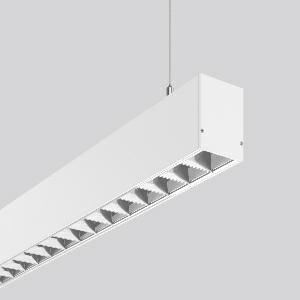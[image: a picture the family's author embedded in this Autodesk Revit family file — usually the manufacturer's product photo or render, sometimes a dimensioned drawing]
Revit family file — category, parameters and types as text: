
# Revit family: less_is_more_50_312342_002_1_76_e1d1
name_source: partatom
category: Lighting Fixtures
units: mm (PartAtom-declared; Revit-internal decimal feet)

## family parameters
Cut with Voids When Loaded = No
Host = Face
Light Source = No
Part Type = Normal
Room Calculation Point = No
Round Connector Dimension = Use Diameter
Shared = No

## types (1)
- LESS IS MORE 50 (1 x LED Modul 840, 5050 lm, 4000)
    Apparent Load = 46 VA
    CIE Flux Codes = 95 100 100 63 100
    Color Rendering = 80
    Color Temperature = 4000
    Default Elevation = 1800 mm
    Description = Series: LESS IS MORE 50
Linear pendant luminaire for aesthetically sophisticated lighting. Housing: extruded aluminium profile, powder-coated. End cap aluminium powder-coated. Canopy made of aluminium, powder-coated. Alea optical system: Reflector structure (ABS, Aluminium-coated, highly polished) with integrated diffuser made of non-yellowing plastic (PMMA) opal for glare-free light at the workstation (screen-compliant according to EN 12464-1). Direct 65%, indirect 35% light emission. Controlled separately. Suitable for pendant. 2-point steel cable suspension freely positionable and infinitely height-adjustable. Special lengths available on request. LED unit with integrated converter interchangeable and removable. Suitable for through-wiring. With sensors or as a safety luminaire on request. 
Colour: traffic white, matt (RAL 9016)
Length: 1127 mm
Width: 57 mm
Height: 75 mm
Suspension length: 2000 mm
Lamp: LED
Socket: without socket
Colour temperature: 4000K
Colour rendering index (CRI): 80
Light source: LED
Socket lamp2: Without base
Colour temperature: 4000K
System power: 46 W
Rated luminous flux: 5050 lm
Luminous efficiency: 110 lm/W
Control gear: Converter, dimmable, DALI
Control gear: Converter, dimmable, DALI
Protection class: I
Type of protection: IP 20
    Height = 75 mm
    Lamp = 1 x LED Modul 840
    Lamp Light Flux = 5050 lm
    Lamp count = 1
    Length = 1127 mm
    Lifetime = 50000 h
    Luminous efficacy = 110 lm/W
    Manufacturer = RZB
    ModVariant = No
    Model = 312342.002.1.76
    Mounting Place = Ceiling
    Mounting Type = Pendant
    Number of Poles = 1
    OnlyDefault = Yes
    Power Factor = 1
    Product Name = LESS IS MORE 50
    Product group = Pendant LED linear luminaires
    ProductGroupID = 907
    Protection Class = Protection class I
    Protection Degree = IP 20
    RLX_Detail_Level = 1
    RLX_Emergency_Light_Flux = 0 lm
    RLX_Emergency_Type = 0
    RLX_Emergency_Type_DB = No
    RlxData = <blob elided: 37445 chars, md5=4f5b8501>
    Socket = socket
    Standby Power = 0 W
    System Light Flux = 5050 lm
    System Power = 46 W
    Type Comments = Product without accessories
    Type Image = 312342.002.jpg
    URL = http://relux.com
    VarID = ---
    Voltage = 230 V
    Voltage Range = 220-240 V
    Weight = 0.00 kg
    Width = 57 mm

## geometry (parser evidence)
native form markers: Blend x4, Sweep x14
no freeform markers — native parametric forms only
